# Revit family: 14260
name_source: partatom
category: Plumbing Fixtures
units: mm (PartAtom-declared; Revit-internal decimal feet)

## family parameters
Always vertical = Yes
Cut with Voids When Loaded = No
Maintain Annotation Orientation = No
OmniClass Number = 23.45.00.00
OmniClass Title = Sanitary, Laundry, and Cleaning Equipment
Part Type = Normal
Room Calculation Point = No
Round Connector Dimension = Use Diameter
Shared = No
Work Plane-Based = Yes

## types (1)
- 14260 - PRESTO
    - Hydraulic supply = 25.00 mm
    -Delivered with = 1 Ball valve / - 1 Remote control for induct mounting 15 to 200mm with clamping nuts / - 1 PVC angled pipe / - 1 Nozzle / - 1 Instruction manual
    > Standards & approvals = Acoustic class II / - Brass body in accordance with EN 1982, EN 12164, EN 12165 / - Molded chrome-plated body in accordance with EN 12540 / - 200-hour neutral salt spray resistant (NSS) in accordance with ISO 9227
    Default Elevation = 1219 mm
    Description = PRESTO 1000 XL TC Induct mounting
    Manufacturer = PRESTO
    Recommended pressure = 3.0 Pa
    URL = https://www.prestodatashare.com
    brand = LES ROBINETS PRESTO
    flow = 6.0 L/s
    flow time = 1.0 s
    min flow = 1.0 L/s
    power = 0 W
    pressure = 5.0 Pa
    ref = 14260 - PRESTO 1000 XL TC Induct mounting

## geometry (parser evidence)
native form markers: Sweep x3
no freeform markers — native parametric forms only
